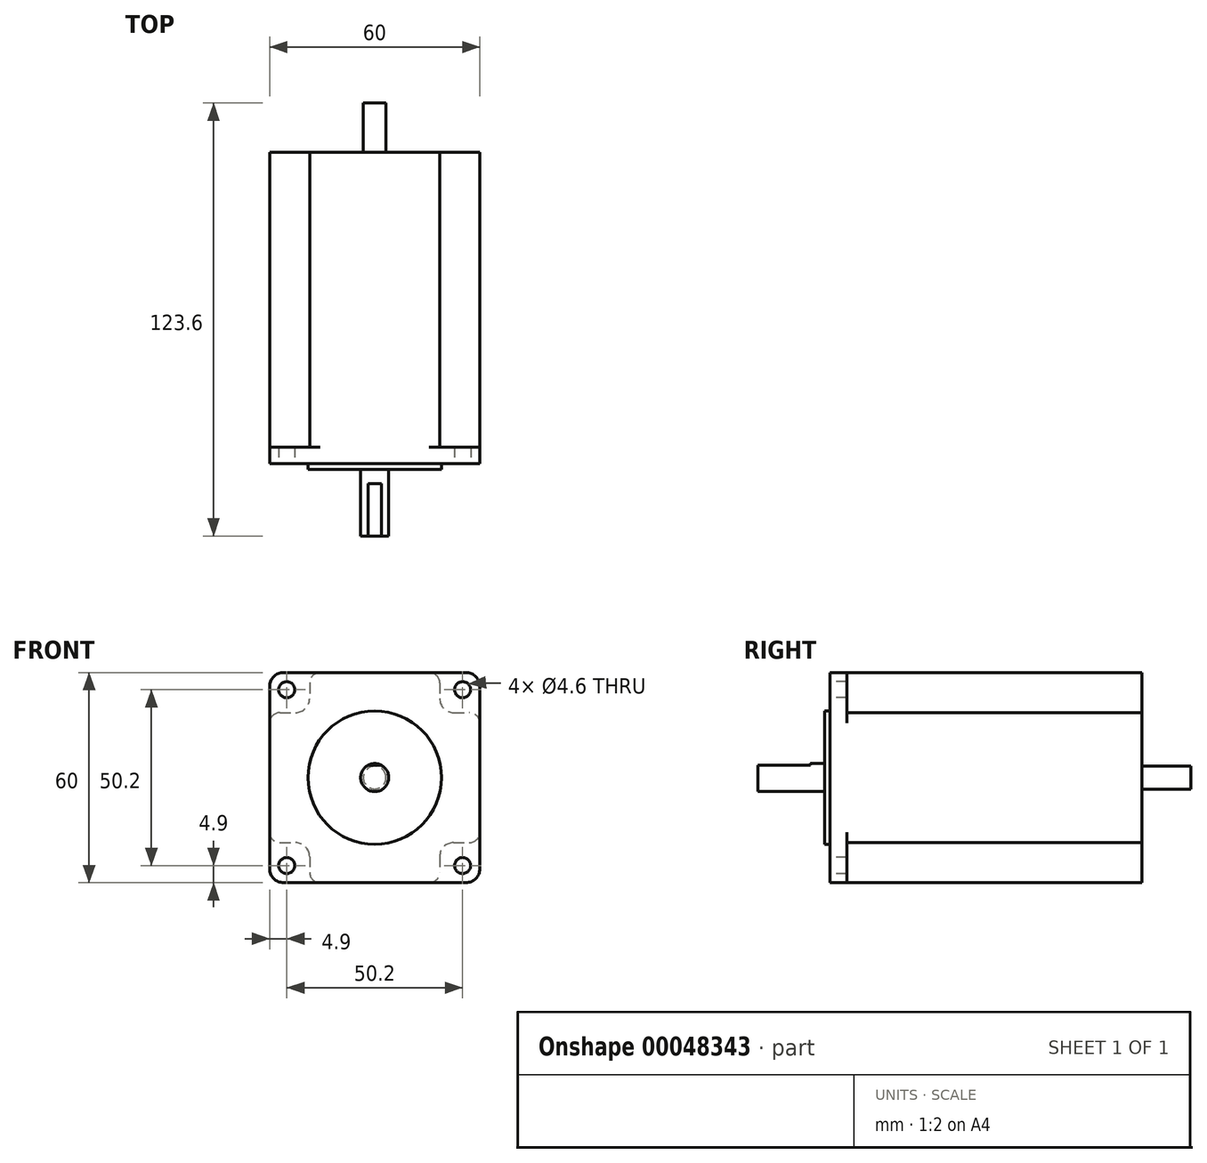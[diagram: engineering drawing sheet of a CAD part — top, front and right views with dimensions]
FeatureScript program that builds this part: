
annotation { "Feature Type Name" : "Feature", "Feature Type Description" : "" }
export const myFeature = defineFeature(function(context is Context, id is Id, definition is map)
    precondition{}
    {
        {
            var Q0;
            Q0=qCreatedBy(makeId("Front.planeOp"),FACE);
            var sketch = newSketch(context, id + "F0", { "sketchPlane" : qUnion([Q0])});
            skLineSegment(sketch, "E0.rect.bottom", {"start": v(-30, 30) * mm, "end": v(30, 30) * mm});
            skLineSegment(sketch, "E0.rect.top", {"start": v(-30, -30) * mm, "end": v(30, -30) * mm});
            skLineSegment(sketch, "E0.rect.left", {"start": v(-30, 30) * mm, "end": v(-30, -30) * mm});
            skLineSegment(sketch, "E0.rect.right", {"start": v(30, 30) * mm, "end": v(30, -30) * mm});
            skPoint(sketch, "E0.rect.middle", {"position": v(0, 0) * mm});
            skCircle(sketch, "E1", {"center": v(0, 0) * mm, "radius": 19.05 * mm});
            skCircle(sketch, "E2", {"center": v(0, 0) * mm, "radius": 4 * mm});
            skCircle(sketch, "E3", {"center": v(-25.1, 25.1) * mm, "radius": 2.3 * mm});
            skCircle(sketch, "E4", {"center": v(25.1, 25.1) * mm, "radius": 2.3 * mm});
            skCircle(sketch, "E5", {"center": v(25.1, -25.1) * mm, "radius": 2.3 * mm});
            skCircle(sketch, "E6", {"center": v(-25.1, -25.1) * mm, "radius": 2.3 * mm});
            skLineSegment(sketch, "E7.rect.bottom", {"start": v(-25.1, 25.1) * mm, "end": v(25.1, 25.1) * mm, "construction": true});
            skLineSegment(sketch, "E7.rect.top", {"start": v(-25.1, -25.1) * mm, "end": v(25.1, -25.1) * mm, "construction": true});
            skLineSegment(sketch, "E7.rect.left", {"start": v(-25.1, 25.1) * mm, "end": v(-25.1, -25.1) * mm, "construction": true});
            skLineSegment(sketch, "E7.rect.right", {"start": v(25.1, 25.1) * mm, "end": v(25.1, -25.1) * mm, "construction": true});
            skSolve(sketch);
        }
        {
            var Q0;
            Q0=makeQuery(id+"F0.imprint","IMPRINT",FACE,{"disambiguationData":[TD([[makeQuery(id+"F0.imprint","IMPRINT",EDGE,{"derivedFrom":sQuery(id+"F0.wireOp",EDGE,"E0.rect.bottom")}),-1.0]])]});
            var Q1;
            Q1=makeQuery(id+"F0.imprint","IMPRINT",FACE,{"disambiguationData":[TD([[makeQuery(id+"F0.imprint","IMPRINT",EDGE,{"derivedFrom":sQuery(id+"F0.wireOp",EDGE,"E1")}),1.0]])]});
            var Q2;
            Q2=makeQuery(id+"F0.imprint","IMPRINT",FACE,{"disambiguationData":[TD([[makeQuery(id+"F0.imprint","IMPRINT",EDGE,{"derivedFrom":sQuery(id+"F0.wireOp",EDGE,"E2")}),1.0]])]});
            extrude(context, id + "F1", {"entities" : qUnion([Q0, Q1, Q2]), "oppositeDirection" : true, "depth" : 4.8 * mm});
        }
        {
            var Q0;
            Q0=makeQuery(id+"F0.imprint","IMPRINT",FACE,{"disambiguationData":[TD([[makeQuery(id+"F0.imprint","IMPRINT",EDGE,{"derivedFrom":sQuery(id+"F0.wireOp",EDGE,"E1")}),1.0]])]});
            extrude(context, id + "F2", {"entities" : qUnion([Q0]), "operationType" : NewBodyOperationType.ADD, "depth" : 1.6 * mm});
        }
        {
            var Q0;
            Q0=makeQuery(id+"F0.imprint","IMPRINT",FACE,{"disambiguationData":[TD([[makeQuery(id+"F0.imprint","IMPRINT",EDGE,{"derivedFrom":sQuery(id+"F0.wireOp",EDGE,"E2")}),1.0]])]});
            extrude(context, id + "F3", {"entities" : qUnion([Q0]), "operationType" : NewBodyOperationType.ADD, "depth" : 20.6 * mm});
        }
        {
            var Q0;
            Q0=makeQuery(id+"F1.opExtrude","SWEPT_EDGE",EDGE,{"disambiguationData":[OSD([sQuery(id+"F0.wireOp",EDGE,"E0.rect.bottom"),sQuery(id+"F0.wireOp",EDGE,"E0.rect.left")])]});
            var Q1;
            Q1=makeQuery(id+"F1.opExtrude","SWEPT_EDGE",EDGE,{"disambiguationData":[OSD([sQuery(id+"F0.wireOp",EDGE,"E0.rect.bottom"),sQuery(id+"F0.wireOp",EDGE,"E0.rect.right")])]});
            var Q2;
            Q2=makeQuery(id+"F1.opExtrude","SWEPT_EDGE",EDGE,{"disambiguationData":[OSD([sQuery(id+"F0.wireOp",EDGE,"E0.rect.top"),sQuery(id+"F0.wireOp",EDGE,"E0.rect.right")])]});
            var Q3;
            Q3=makeQuery(id+"F1.opExtrude","SWEPT_EDGE",EDGE,{"disambiguationData":[OSD([sQuery(id+"F0.wireOp",EDGE,"E0.rect.top"),sQuery(id+"F0.wireOp",EDGE,"E0.rect.left")])]});
            fillet(context, id + "F4", {"entities" : qUnion([Q0, Q1, Q2, Q3]), "radius" : 4 * mm, "tangentPropagation" : true, "allowEdgeOverflow" : false});
        }
        {
            var Q0;
            Q0=makeQuery(id+"F1.opExtrude","SWEPT_FACE",FACE,{"disambiguationData":[OSD([sQuery(id+"F0.wireOp",EDGE,"E0.rect.left")])]});
            var sketch = newSketch(context, id + "F5", { "sketchPlane" : qUnion([Q0])});
            skLineSegment(sketch, "E8", {"start": v(1.6, 4) * mm, "end": v(20.6, 4) * mm});
            skLineSegment(sketch, "E9.0", {"start": v(20.6, 4) * mm, "end": v(20.6, -4) * mm});
            skLineSegment(sketch, "E10", {"start": v(5.6, 4) * mm, "end": v(5.6, 3.5) * mm});
            skLineSegment(sketch, "E11", {"start": v(5.6, 3.5) * mm, "end": v(20.6, 3.5) * mm});
            skSolve(sketch);
        }
        {
            var Q0;
            {var subQ1=sQuery(id+"F5.wireOp",EDGE,"E10");Q0=makeQuery(id+"F5.imprint","IMPRINT",FACE,{"disambiguationData":[TD([[makeQuery(id+"F5.imprint","IMPRINT",EDGE,{"derivedFrom":subQ1}),1.0]])]});}
            extrude(context, id + "F6", {"entities" : qUnion([Q0]), "operationType" : NewBodyOperationType.REMOVE, "endBound" : BoundingType.THROUGH_ALL, "oppositeDirection" : true, "depth" : 25 * mm});
        }
        {
            var Q0;
            Q0=qCreatedBy(makeId("Front.planeOp"),FACE);
            var sketch = newSketch(context, id + "F7", { "sketchPlane" : qUnion([Q0])});
            skPoint(sketch, "E12.rect.middle", {"position": v(0, 0.02) * mm});
            skPoint(sketch, "E13", {"position": v(0, 0) * mm});
            skLineSegment(sketch, "E14.rect.bottom", {"start": v(-18.57, 30) * mm, "end": v(18.57, 30) * mm});
            skLineSegment(sketch, "E14.rect.top", {"start": v(-18.57, -30) * mm, "end": v(18.57, -30) * mm});
            skLineSegment(sketch, "E14.rect.left", {"start": v(-18.57, 30) * mm, "end": v(-18.57, -30) * mm});
            skLineSegment(sketch, "E14.rect.right", {"start": v(18.57, 30) * mm, "end": v(18.57, -30) * mm});
            skLineSegment(sketch, "E15.rect.bottom", {"start": v(-30, 18.57) * mm, "end": v(30, 18.57) * mm});
            skLineSegment(sketch, "E15.rect.top", {"start": v(-30, -18.57) * mm, "end": v(30, -18.57) * mm});
            skLineSegment(sketch, "E15.rect.left", {"start": v(-30, 18.57) * mm, "end": v(-30, -18.57) * mm});
            skLineSegment(sketch, "E15.rect.right", {"start": v(30, 18.57) * mm, "end": v(30, -18.57) * mm});
            skSolve(sketch);
        }
        {
            var Q0;
            Q0=qSketchRegion(id+"F7",true);
            extrude(context, id + "F8", {"entities" : qUnion([Q0]), "operationType" : NewBodyOperationType.ADD, "oppositeDirection" : true, "depth" : 89 * mm});
        }
        {
            var Q0;
            Q0=makeQuery(id+"F8.opExtrude","SWEPT_EDGE",EDGE,{"disambiguationData":[OSD([sQuery(id+"F7.wireOp",EDGE,"E14.rect.right"),sQuery(id+"F7.wireOp",EDGE,"E15.rect.bottom")])]});
            var Q1;
            Q1=makeQuery(id+"F8.opExtrude","SWEPT_EDGE",EDGE,{"disambiguationData":[OSD([sQuery(id+"F7.wireOp",EDGE,"E14.rect.left"),sQuery(id+"F7.wireOp",EDGE,"E15.rect.bottom")])]});
            var Q2;
            Q2=makeQuery(id+"F8.opExtrude","SWEPT_EDGE",EDGE,{"disambiguationData":[OSD([sQuery(id+"F7.wireOp",EDGE,"E14.rect.left"),sQuery(id+"F7.wireOp",EDGE,"E15.rect.top")])]});
            var Q3;
            Q3=makeQuery(id+"F8.opExtrude","SWEPT_EDGE",EDGE,{"disambiguationData":[OSD([sQuery(id+"F7.wireOp",EDGE,"E14.rect.right"),sQuery(id+"F7.wireOp",EDGE,"E15.rect.top")])]});
            fillet(context, id + "F9", {"entities" : qUnion([Q0, Q1, Q2, Q3]), "radius" : 4 * mm, "tangentPropagation" : true, "allowEdgeOverflow" : false});
        }
        {
            var Q0;
            Q0=makeQuery(id+"F8.opExtrude","SWEPT_EDGE",EDGE,{"disambiguationData":[OSD([sQuery(id+"F7.wireOp",EDGE,"E14.rect.bottom"),sQuery(id+"F7.wireOp",EDGE,"E14.rect.right")])]});
            var Q1;
            Q1=makeQuery(id+"F8.opExtrude","SWEPT_EDGE",EDGE,{"disambiguationData":[OSD([sQuery(id+"F7.wireOp",EDGE,"E15.rect.bottom"),sQuery(id+"F7.wireOp",EDGE,"E15.rect.right")])]});
            var Q2;
            Q2=makeQuery(id+"F8.opExtrude","SWEPT_EDGE",EDGE,{"disambiguationData":[OSD([sQuery(id+"F7.wireOp",EDGE,"E15.rect.top"),sQuery(id+"F7.wireOp",EDGE,"E15.rect.right")])]});
            var Q3;
            Q3=makeQuery(id+"F8.opExtrude","SWEPT_EDGE",EDGE,{"disambiguationData":[OSD([sQuery(id+"F7.wireOp",EDGE,"E14.rect.top"),sQuery(id+"F7.wireOp",EDGE,"E14.rect.right")])]});
            var Q4;
            Q4=makeQuery(id+"F8.opExtrude","SWEPT_EDGE",EDGE,{"disambiguationData":[OSD([sQuery(id+"F7.wireOp",EDGE,"E14.rect.top"),sQuery(id+"F7.wireOp",EDGE,"E14.rect.left")])]});
            var Q5;
            Q5=makeQuery(id+"F8.opExtrude","SWEPT_EDGE",EDGE,{"disambiguationData":[OSD([sQuery(id+"F7.wireOp",EDGE,"E15.rect.top"),sQuery(id+"F7.wireOp",EDGE,"E15.rect.left")])]});
            var Q6;
            Q6=makeQuery(id+"F8.opExtrude","SWEPT_EDGE",EDGE,{"disambiguationData":[OSD([sQuery(id+"F7.wireOp",EDGE,"E15.rect.bottom"),sQuery(id+"F7.wireOp",EDGE,"E15.rect.left")])]});
            var Q7;
            Q7=makeQuery(id+"F8.opExtrude","SWEPT_EDGE",EDGE,{"disambiguationData":[OSD([sQuery(id+"F7.wireOp",EDGE,"E14.rect.bottom"),sQuery(id+"F7.wireOp",EDGE,"E14.rect.left")])]});
            fillet(context, id + "F10", {"entities" : qUnion([Q0, Q1, Q2, Q3, Q4, Q5, Q6, Q7]), "radius" : 3 * mm, "tangentPropagation" : true, "allowEdgeOverflow" : false});
        }
        {
            var Q0;
            Q0=makeQuery(id+"F8.opExtrude","CAP_FACE",FACE,{"disambiguationData":[OSD([sQuery(id+"F7.wireOp",EDGE,"E14.rect.bottom"),sQuery(id+"F7.wireOp",EDGE,"E14.rect.top"),sQuery(id+"F7.wireOp",EDGE,"E14.rect.left"),sQuery(id+"F7.wireOp",EDGE,"E14.rect.right"),sQuery(id+"F7.wireOp",EDGE,"E15.rect.bottom"),sQuery(id+"F7.wireOp",EDGE,"E15.rect.top"),sQuery(id+"F7.wireOp",EDGE,"E15.rect.left"),sQuery(id+"F7.wireOp",EDGE,"E15.rect.right")])],"isStart":false});
            var sketch = newSketch(context, id + "F11", { "sketchPlane" : qUnion([Q0])});
            skLineSegment(sketch, "E16", {"start": v(-30, 0) * mm, "end": v(30, 0) * mm, "construction": true});
            skLineSegment(sketch, "E17", {"start": v(0, 30) * mm, "end": v(0, -30) * mm, "construction": true});
            skCircle(sketch, "E18", {"center": v(0, 0) * mm, "radius": 3.25 * mm});
            skSolve(sketch);
        }
        {
            var Q0;
            Q0=makeQuery(id+"F11.imprint","IMPRINT",FACE,{"disambiguationData":[TD([[makeQuery(id+"F11.imprint","IMPRINT",EDGE,{"derivedFrom":sQuery(id+"F11.wireOp",EDGE,"E18")}),1.0]])]});
            var Q1;
            Q1=sQuery(id+"F11.wireOp",EDGE,"E18");
            extrude(context, id + "F12", {"entities" : qUnion([Q0]), "operationType" : NewBodyOperationType.ADD, "surfaceEntities" : qUnion([Q1]), "depth" : 14 * mm});
        }
    });
